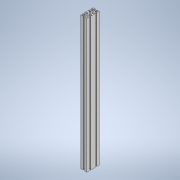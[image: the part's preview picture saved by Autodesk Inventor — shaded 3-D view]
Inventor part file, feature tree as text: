
AUTODESK INVENTOR PART (.ipt)
format: ipt  version: 2022 (Build 260153000, 153)  size: 193,024 bytes
history: native  units: in
note: dims shown in document units (in); Inventor stores cm internally (conversion verified against a paired STEP export)
features: sketch x3, plane x1, extrude x1, hole x1
ambient origin geometry x8: Origin, YZ Plane, XZ Plane, XY Plane, X Axis, Y Axis, Z Axis, Center Point
bodies: Body1 (feature_tree)
feature tree (6):
  plane  "Work Plane1"
  extrude  "Extrusion1"  Depth=16.9685in TaperAngle=0.0deg
  hole  "Hole1"  [1 undecoded]
  sketch  "Sketch1"  dims[d0=16.9685in d1=16.9685in d2=0.0in]
  sketch  "Sketch2"  dims[d3=0.1575in d4=0.2362in d5=0.1575in d6=0.0787in d7=90.0deg d8=0.315in d9=0.8108in]
  sketch  "Sketch3"  dims[d10=0.1575in d11=0.2362in d12=0.1575in d13=0.0787in d14=90.0deg d15=0.315in d16=0.8108in]
note: 1 required parameter value undecoded (feature->parameter linkage not recoverable at this tier; creation-order binding heuristic only, values carry confidence <= 0.55)
